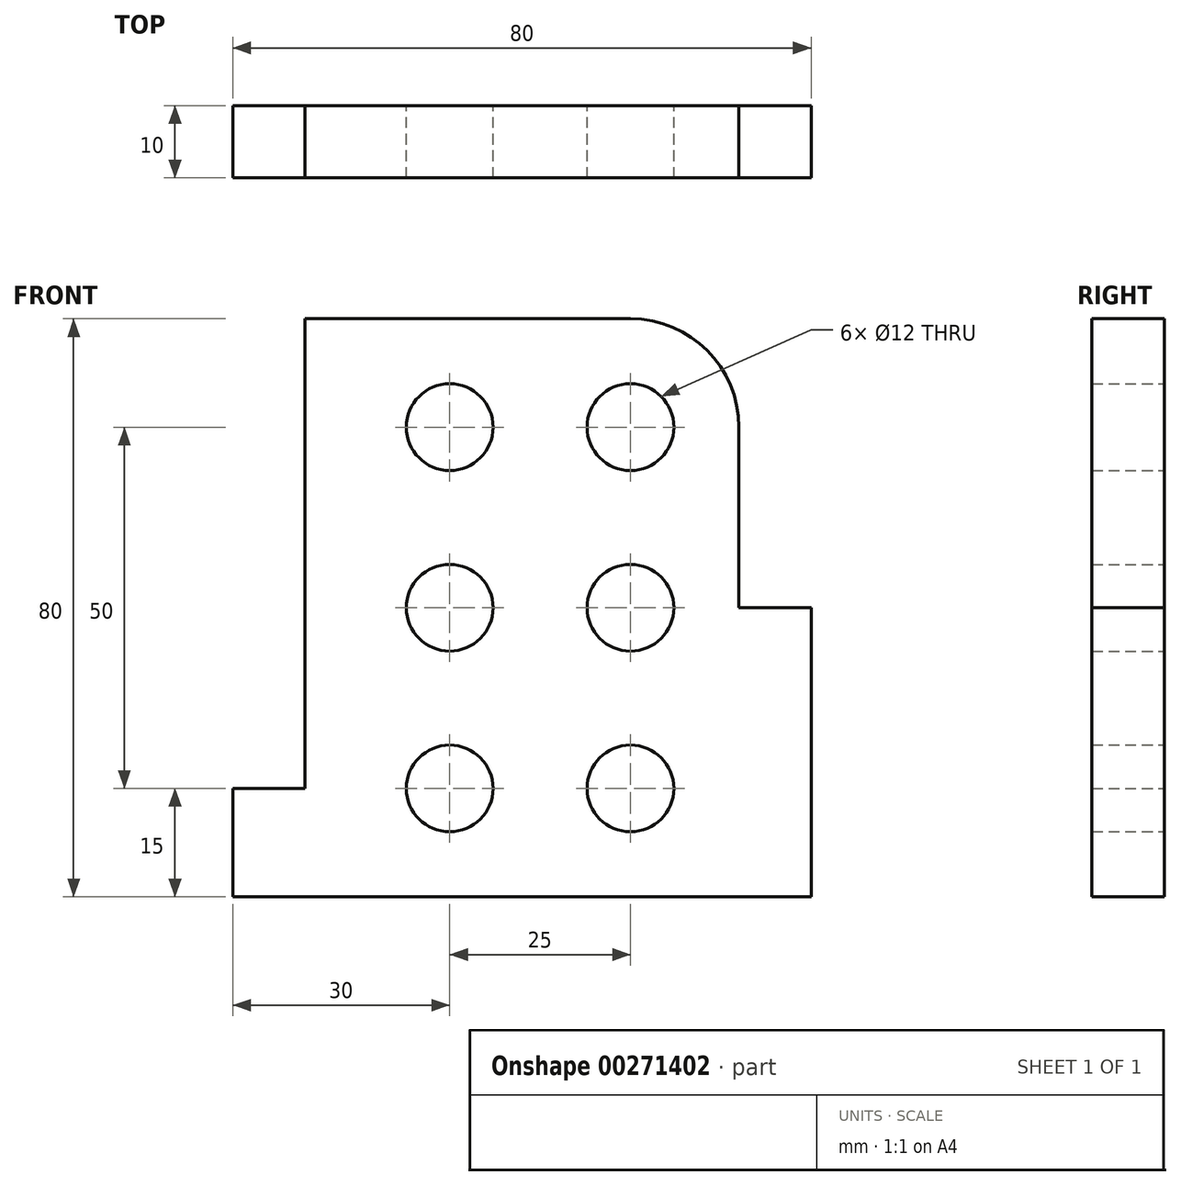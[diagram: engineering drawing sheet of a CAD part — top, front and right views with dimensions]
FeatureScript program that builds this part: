
annotation { "Feature Type Name" : "Feature", "Feature Type Description" : "" }
export const myFeature = defineFeature(function(context is Context, id is Id, definition is map)
    precondition{}
    {
        {
            var Q0;
            Q0=qCreatedBy(makeId("Front.planeOp"),FACE);
            var sketch = newSketch(context, id + "F0", { "sketchPlane" : qUnion([Q0])});
            skLineSegment(sketch, "E0", {"start": v(0, 0) * mm, "end": v(80, 0) * mm});
            skLineSegment(sketch, "E1", {"start": v(0, 0) * mm, "end": v(0, 15) * mm});
            skLineSegment(sketch, "E2", {"start": v(0, 15) * mm, "end": v(10, 15) * mm});
            skLineSegment(sketch, "E3", {"start": v(10, 15) * mm, "end": v(10, 80) * mm});
            skLineSegment(sketch, "E4", {"start": v(10, 80) * mm, "end": v(55, 80) * mm});
            skCircle(sketch, "E5", {"center": v(30, 15) * mm, "radius": 6 * mm});
            skCircle(sketch, "E6", {"center": v(55, 15) * mm, "radius": 6 * mm});
            skCircle(sketch, "E7", {"center": v(30, 40) * mm, "radius": 6 * mm});
            skCircle(sketch, "E8", {"center": v(30, 65) * mm, "radius": 6 * mm});
            skCircle(sketch, "E9", {"center": v(55, 65) * mm, "radius": 6 * mm});
            skLineSegment(sketch, "E10", {"start": v(80, 0) * mm, "end": v(80, 40) * mm});
            skLineSegment(sketch, "E11", {"start": v(80, 40) * mm, "end": v(70, 40) * mm});
            skLineSegment(sketch, "E12", {"start": v(70, 40) * mm, "end": v(70, 65) * mm});
            skCircle(sketch, "E13", {"center": v(55, 40) * mm, "radius": 6 * mm});
            skArc(sketch, "E14", {"start": v(55, 80) * mm, "mid": v(65.6, 75.6) * mm, "end": v(70, 65) * mm});
            skSolve(sketch);
        }
        {
            var Q0;
            Q0 = qSketchRegion(id + "F0", true);
            extrude(context, id + "F1", {"entities" : qUnion([Q0]), "depth" : 10 * mm});
        }
    });
